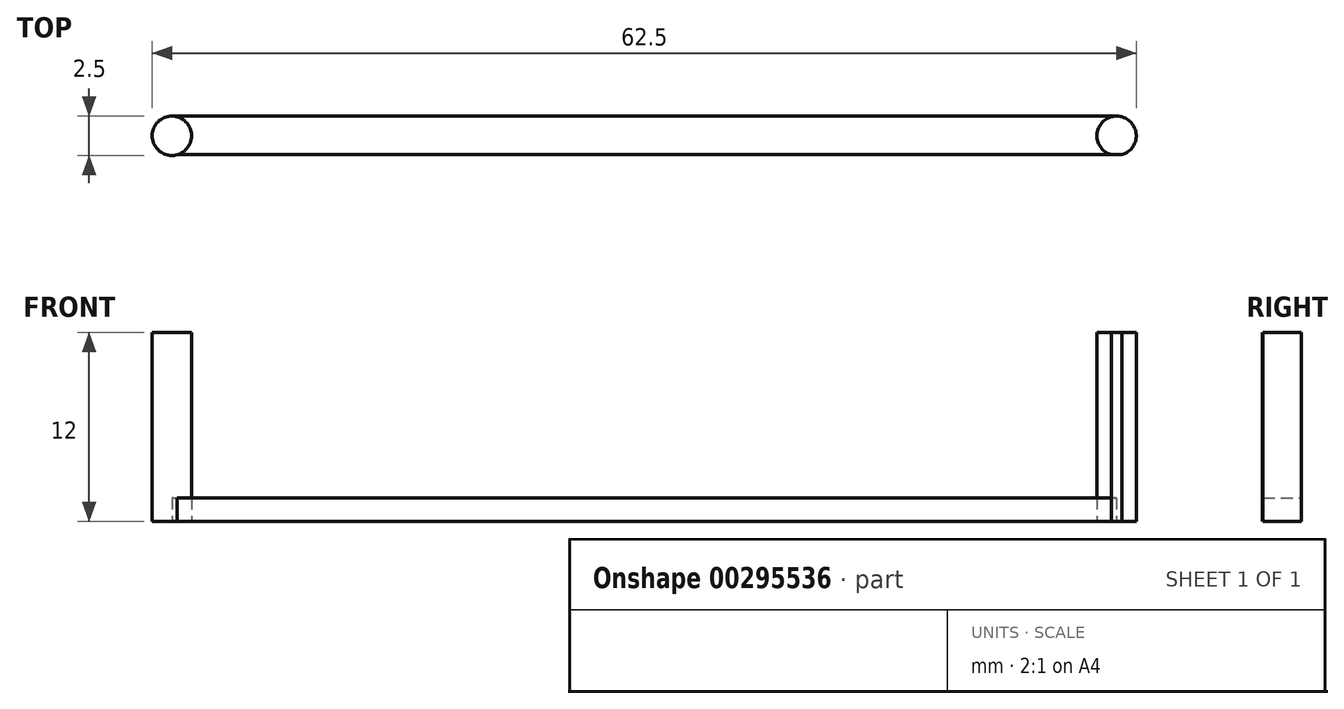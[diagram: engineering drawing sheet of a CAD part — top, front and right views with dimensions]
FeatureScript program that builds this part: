
annotation { "Feature Type Name" : "Feature", "Feature Type Description" : "" }
export const myFeature = defineFeature(function(context is Context, id is Id, definition is map)
    precondition{}
    {
        {
            var Q0;
            Q0=qCreatedBy(makeId("Top.planeOp"),FACE);
            var sketch = newSketch(context, id + "F0", { "sketchPlane" : qUnion([Q0])});
            skCircle(sketch, "E0", {"center": v(0, 0) * mm, "radius": 1.25 * mm});
            skCircle(sketch, "E1", {"center": v(60, 0) * mm, "radius": 1.25 * mm});
            skLineSegment(sketch, "E2.top", {"start": v(0, 0) * mm, "end": v(60, 0) * mm});
            skLineSegment(sketch, "E3.bottom", {"start": v(0, 1.25) * mm, "end": v(60.33, 1.25) * mm});
            skLineSegment(sketch, "E3.top", {"start": v(0, -1.2) * mm, "end": v(60.33, -1.2) * mm});
            skLineSegment(sketch, "E3.left", {"start": v(0, 1.25) * mm, "end": v(0, -1.2) * mm});
            skLineSegment(sketch, "E3.right", {"start": v(60.33, 1.25) * mm, "end": v(60.33, -1.2) * mm});
            skSolve(sketch);
        }
        {
            var Q0;
            {var subQ0=sQuery(id+"F0.wireOp",EDGE,"E3.left");var subQ3=sQuery(id+"F0.wireOp",EDGE,"E3.top");var subQ6=makeQuery(id+"F0.imprint","INTERSECT",VERTEX,{"derivedFrom":[subQ3,subQ0]});Q0=makeQuery(id+"F0.imprint","IMPRINT",FACE,{"disambiguationData":[TD([[makeQuery(id+"F0.imprint","IMPRINT",EDGE,{"disambiguationData":[TD([[subQ6,-1.0]])],"derivedFrom":subQ3}),-1.0]])]});}
            var Q1;
            {var subQ0=sQuery(id+"F0.wireOp",EDGE,"E3.top");var subQ1=sQuery(id+"F0.wireOp",EDGE,"E0");var subQ2=makeQuery(id+"F0.imprint","INTERSECT",VERTEX,{"derivedFrom":[subQ1,subQ0]});Q1=makeQuery(id+"F0.imprint","IMPRINT",FACE,{"disambiguationData":[TD([[makeQuery(id+"F0.imprint","IMPRINT",EDGE,{"disambiguationData":[TD([[subQ2,-1.0]])],"derivedFrom":subQ1}),1.0]])]});}
            var Q2;
            {var subQ0=sQuery(id+"F0.wireOp",EDGE,"E3.left");var subQ3=sQuery(id+"F0.wireOp",EDGE,"E2.top");var subQ5=makeQuery(id+"F0.imprint","INTERSECT",VERTEX,{"derivedFrom":[subQ3,subQ0]});Q2=makeQuery(id+"F0.imprint","IMPRINT",FACE,{"disambiguationData":[TD([[makeQuery(id+"F0.imprint","IMPRINT",EDGE,{"disambiguationData":[TD([[subQ5,-1.0]])],"derivedFrom":subQ3}),1.0]])]});}
            var Q3;
            {var subQ0=sQuery(id+"F0.wireOp",EDGE,"E3.right");var subQ1=sQuery(id+"F0.wireOp",EDGE,"E1");var subQ3=makeQuery(id+"F0.imprint","INTERSECT",VERTEX,{"derivedFrom":[subQ1,subQ0]});Q3=makeQuery(id+"F0.imprint","IMPRINT",FACE,{"disambiguationData":[TD([[makeQuery(id+"F0.imprint","IMPRINT",EDGE,{"disambiguationData":[TD([[subQ3,1.0]])],"derivedFrom":subQ1}),1.0]])]});}
            var Q4;
            {var subQ0=sQuery(id+"F0.wireOp",EDGE,"E1");var subQ6=makeQuery(id+"F0.imprint","INTERSECT",VERTEX,{"derivedFrom":[subQ0,sQuery(id+"F0.wireOp",EDGE,"E3.bottom")]});Q4=makeQuery(id+"F0.imprint","IMPRINT",FACE,{"disambiguationData":[TD([[makeQuery(id+"F0.imprint","IMPRINT",EDGE,{"disambiguationData":[TD([[subQ6,1.0]])],"derivedFrom":subQ0}),1.0]])]});}
            extrude(context, id + "F1", {"entities" : qUnion([Q0, Q1, Q2, Q3, Q4]), "depth" : 12 * mm});
        }
        {
            var Q0;
            {var subQ0=sQuery(id+"F0.wireOp",EDGE,"E3.bottom");var subQ5=sQuery(id+"F0.wireOp",EDGE,"E1");var subQ6=makeQuery(id+"F0.imprint","INTERSECT",VERTEX,{"derivedFrom":[subQ5,subQ0]});Q0=makeQuery(id+"F0.imprint","IMPRINT",FACE,{"disambiguationData":[TD([[makeQuery(id+"F0.imprint","IMPRINT",EDGE,{"disambiguationData":[TD([[subQ6,-1.0]])],"derivedFrom":subQ5}),-1.0]])]});}
            var Q1;
            {var subQ0=sQuery(id+"F0.wireOp",EDGE,"E3.top");var subQ1=sQuery(id+"F0.wireOp",EDGE,"E0");var subQ2=makeQuery(id+"F0.imprint","INTERSECT",VERTEX,{"derivedFrom":[subQ1,subQ0]});Q1=makeQuery(id+"F0.imprint","IMPRINT",FACE,{"disambiguationData":[TD([[makeQuery(id+"F0.imprint","IMPRINT",EDGE,{"disambiguationData":[TD([[subQ2,-1.0]])],"derivedFrom":subQ1}),-1.0]])]});}
            extrude(context, id + "F2", {"entities" : qUnion([Q0, Q1]), "depth" : 1.5 * mm});
        }
    });
